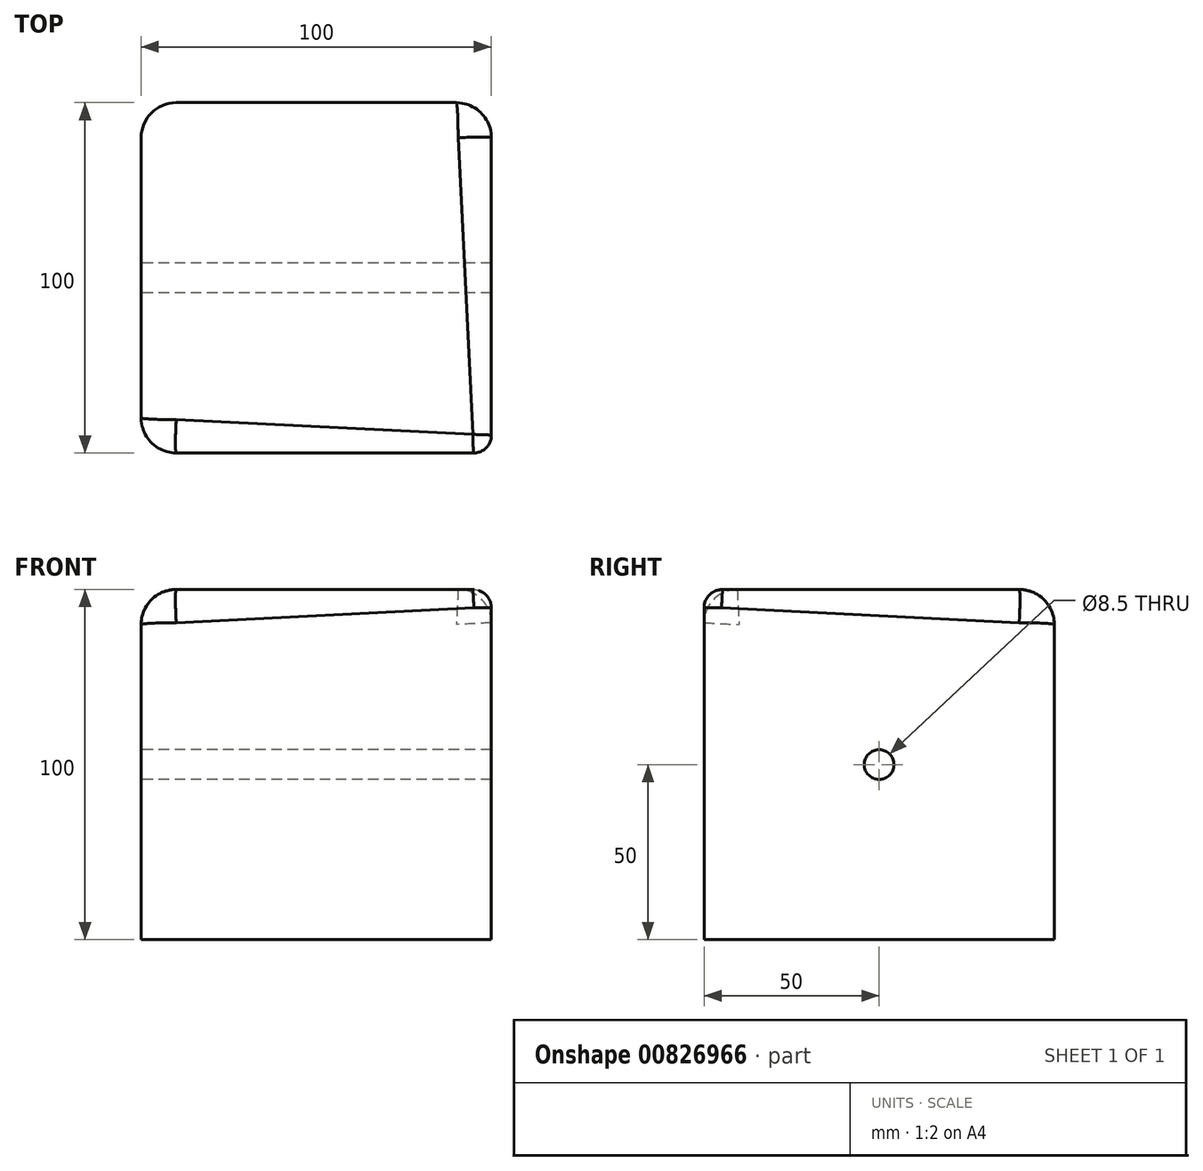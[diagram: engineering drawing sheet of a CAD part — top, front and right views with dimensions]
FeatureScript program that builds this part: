
annotation { "Feature Type Name" : "Feature", "Feature Type Description" : "" }
export const myFeature = defineFeature(function(context is Context, id is Id, definition is map)
    precondition{}
    {
        {
            var Q0;
            Q0=qCreatedBy(makeId("Top.planeOp"),FACE);
            var sketch = newSketch(context, id + "F0", { "sketchPlane" : qUnion([Q0])});
            skLineSegment(sketch, "E0.bottom", {"start": v(50, 50) * mm, "end": v(-50, 50) * mm});
            skLineSegment(sketch, "E0.top", {"start": v(50, -50) * mm, "end": v(-50, -50) * mm});
            skLineSegment(sketch, "E0.left", {"start": v(50, 50) * mm, "end": v(50, -50) * mm});
            skLineSegment(sketch, "E0.right", {"start": v(-50, 50) * mm, "end": v(-50, -50) * mm});
            skPoint(sketch, "E0.middle", {"position": v(0, 0) * mm});
            skSolve(sketch);
        }
        {
            var Q0;
            Q0=makeQuery(id+"F0.imprint","IMPRINT",FACE,{"disambiguationData":[TD([[makeQuery(id+"F0.imprint","IMPRINT",EDGE,{"derivedFrom":sQuery(id+"F0.wireOp",EDGE,"E0.bottom")}),1.0]])]});
            extrude(context, id + "F1", {"entities" : qUnion([Q0]), "depth" : 100 * mm, "offsetDistance" : 25 * mm});
        }
        {
            var Q0;
            Q0=makeQuery(id+"F1.opExtrude","SWEPT_FACE",FACE,{"disambiguationData":[OSD([sQuery(id+"F0.wireOp",EDGE,"E0.left")])]});
            var sketch = newSketch(context, id + "F2", { "sketchPlane" : qUnion([Q0])});
            skArc(sketch, "E1", {"start": v(-45, 100) * mm, "mid": v(-48.54, 98.54) * mm, "end": v(-50, 95) * mm});
            skLineSegment(sketch, "E2", {"start": v(-45, 100) * mm, "end": v(-50, 100) * mm});
            skLineSegment(sketch, "E3", {"start": v(-50, 100) * mm, "end": v(-50, 95) * mm});
            skSolve(sketch);
        }
        {
            var Q0;
            Q0=makeQuery(id+"F1.opExtrude","SWEPT_FACE",FACE,{"disambiguationData":[OSD([sQuery(id+"F0.wireOp",EDGE,"E0.right")])]});
            var sketch = newSketch(context, id + "F3", { "sketchPlane" : qUnion([Q0])});
            skArc(sketch, "E4", {"start": v(50, 90) * mm, "mid": v(47.07, 97.07) * mm, "end": v(40, 100) * mm});
            skLineSegment(sketch, "E5", {"start": v(40, 100) * mm, "end": v(50, 100) * mm});
            skLineSegment(sketch, "E6", {"start": v(50, 100) * mm, "end": v(50, 90) * mm});
            skSolve(sketch);
        }
        {
            var Q1;
            Q1=makeQuery(id+"F3.imprint","IMPRINT",FACE,{"disambiguationData":[TD([[makeQuery(id+"F3.imprint","IMPRINT",EDGE,{"derivedFrom":sQuery(id+"F3.wireOp",EDGE,"E4")}),-1.0]])]});
            var Q2;
            Q2=makeQuery(id+"F2.imprint","IMPRINT",FACE,{"disambiguationData":[TD([[makeQuery(id+"F2.imprint","IMPRINT",EDGE,{"derivedFrom":sQuery(id+"F2.wireOp",EDGE,"E1")}),-1.0]])]});
            loft(context, id + "F4", {"operationType" : NewBodyOperationType.REMOVE, "sheetProfilesArray" : [{ "sheetProfileEntities" : qUnion([Q1]) }, { "sheetProfileEntities" : qUnion([Q2]) }]});
        }
        {
            var Q0;
            Q0=makeQuery(id+"F1.opExtrude","SWEPT_FACE",FACE,{"disambiguationData":[OSD([sQuery(id+"F0.wireOp",EDGE,"E0.top")])]});
            var sketch = newSketch(context, id + "F5", { "sketchPlane" : qUnion([Q0])});
            skFitSpline(sketch, "E7.0", {"points": [v(-50, 100) * mm, v(-16.67, 100) * mm, v(16.67, 100) * mm, v(50, 100) * mm]});
            skFitSpline(sketch, "E8.0", {"points": [v(50, 95) * mm, v(50, 96.67) * mm, v(50, 98.33) * mm, v(50, 100) * mm]});
            skArc(sketch, "E9", {"start": v(50, 95) * mm, "mid": v(48.54, 98.54) * mm, "end": v(45, 100) * mm});
            skSolve(sketch);
        }
        {
            var Q0;
            Q0=makeQuery(id+"F1.opExtrude","SWEPT_FACE",FACE,{"disambiguationData":[OSD([sQuery(id+"F0.wireOp",EDGE,"E0.bottom")])]});
            var sketch = newSketch(context, id + "F6", { "sketchPlane" : qUnion([Q0])});
            skArc(sketch, "E10", {"start": v(-40, 100) * mm, "mid": v(-47.07, 97.07) * mm, "end": v(-50, 90) * mm});
            skLineSegment(sketch, "E11", {"start": v(-40, 100) * mm, "end": v(-50, 100) * mm});
            skLineSegment(sketch, "E12", {"start": v(-50, 100) * mm, "end": v(-50, 90) * mm});
            skSolve(sketch);
        }
        {
            var Q1;
            Q1=makeQuery(id+"F6.imprint","IMPRINT",FACE,{"disambiguationData":[TD([[makeQuery(id+"F6.imprint","IMPRINT",EDGE,{"derivedFrom":sQuery(id+"F6.wireOp",EDGE,"E10")}),-1.0]])]});
            var Q2;
            {var subQ0=sQuery(id+"F5.wireOp",EDGE,"E8.0");Q2=makeQuery(id+"F5.imprint","IMPRINT",FACE,{"disambiguationData":[TD([[makeQuery(id+"F5.imprint","IMPRINT",EDGE,{"derivedFrom":subQ0}),1.0]])]});}
            loft(context, id + "F7", {"operationType" : NewBodyOperationType.REMOVE, "sheetProfilesArray" : [{ "sheetProfileEntities" : qUnion([Q1]) }, { "sheetProfileEntities" : qUnion([Q2]) }]});
        }
        {
            var Q0;
            Q0=makeQuery(id+"F1.opExtrude","SWEPT_EDGE",EDGE,{"disambiguationData":[OSD([sQuery(id+"F0.wireOp",EDGE,"E0.top"),sQuery(id+"F0.wireOp",EDGE,"E0.left")])]});
            fillet(context, id + "F8", {"entities" : qUnion([Q0]), "radius" : 5 * mm, "tangentPropagation" : true, "allowEdgeOverflow" : false});
        }
        {
            var Q0;
            Q0=makeQuery(id+"F1.opExtrude","CAP_EDGE",EDGE,{"disambiguationData":[OSD([sQuery(id+"F0.wireOp",EDGE,"E0.bottom")])],"isStart":false});
            var Q1;
            Q1=makeQuery(id+"F1.opExtrude","CAP_EDGE",EDGE,{"disambiguationData":[OSD([sQuery(id+"F0.wireOp",EDGE,"E0.right")])],"isStart":false});
            var Q2;
            Q2=makeQuery(id+"F1.opExtrude","SWEPT_EDGE",EDGE,{"disambiguationData":[OSD([sQuery(id+"F0.wireOp",EDGE,"E0.bottom"),sQuery(id+"F0.wireOp",EDGE,"E0.right")])]});
            fillet(context, id + "F9", {"entities" : qUnion([Q0, Q1, Q2]), "radius" : 10 * mm, "tangentPropagation" : true, "allowEdgeOverflow" : false});
        }
        {
            var Q0;
            Q0=makeQuery(id+"F1.opExtrude","SWEPT_FACE",FACE,{"disambiguationData":[OSD([sQuery(id+"F0.wireOp",EDGE,"E0.right")])]});
            var sketch = newSketch(context, id + "F10", { "sketchPlane" : qUnion([Q0])});
            skPoint(sketch, "E13", {"position": v(0, 50) * mm});
            skSolve(sketch);
        }
        {
            var Q0;
            Q0=sQuery(id+"F10.wireOp",VERTEX,"E13");
            var Q1;
            Q1=makeQuery(id+"F1.opExtrude","SWEPT_BODY",BODY,{"disambiguationData":[OSD([sQuery(id+"F0.wireOp",EDGE,"E0.bottom"),sQuery(id+"F0.wireOp",EDGE,"E0.top"),sQuery(id+"F0.wireOp",EDGE,"E0.left"),sQuery(id+"F0.wireOp",EDGE,"E0.right")])]});
            hole(context, id + "F11", {"style" : HoleStyle.SIMPLE, "endStyle" : HoleEndStyle.THROUGH, "standardTappedOrClearance" : lookupTablePath({ "standard" : "ISO", "engagement" : "75%", "pitch" : "1.5 mm", "size" : "M10", "type" : "Tapped" }), "standardBlindInLast" : lookupTablePath({ "standard" : "ISO", "engagement" : "75%", "pitch" : "1.5 mm", "size" : "M10", "type" : "Tapped" }), "holeDiameter" : 8.5 * mm, "majorDiameter" : 10 * mm, "showTappedDepth" : true, "isTappedThrough" : true, "tappedDepth" : 12 * mm, "tapClearance" : 3, "locations" : qUnion([Q0]), "scope" : qUnion([Q1])});
        }
    });
